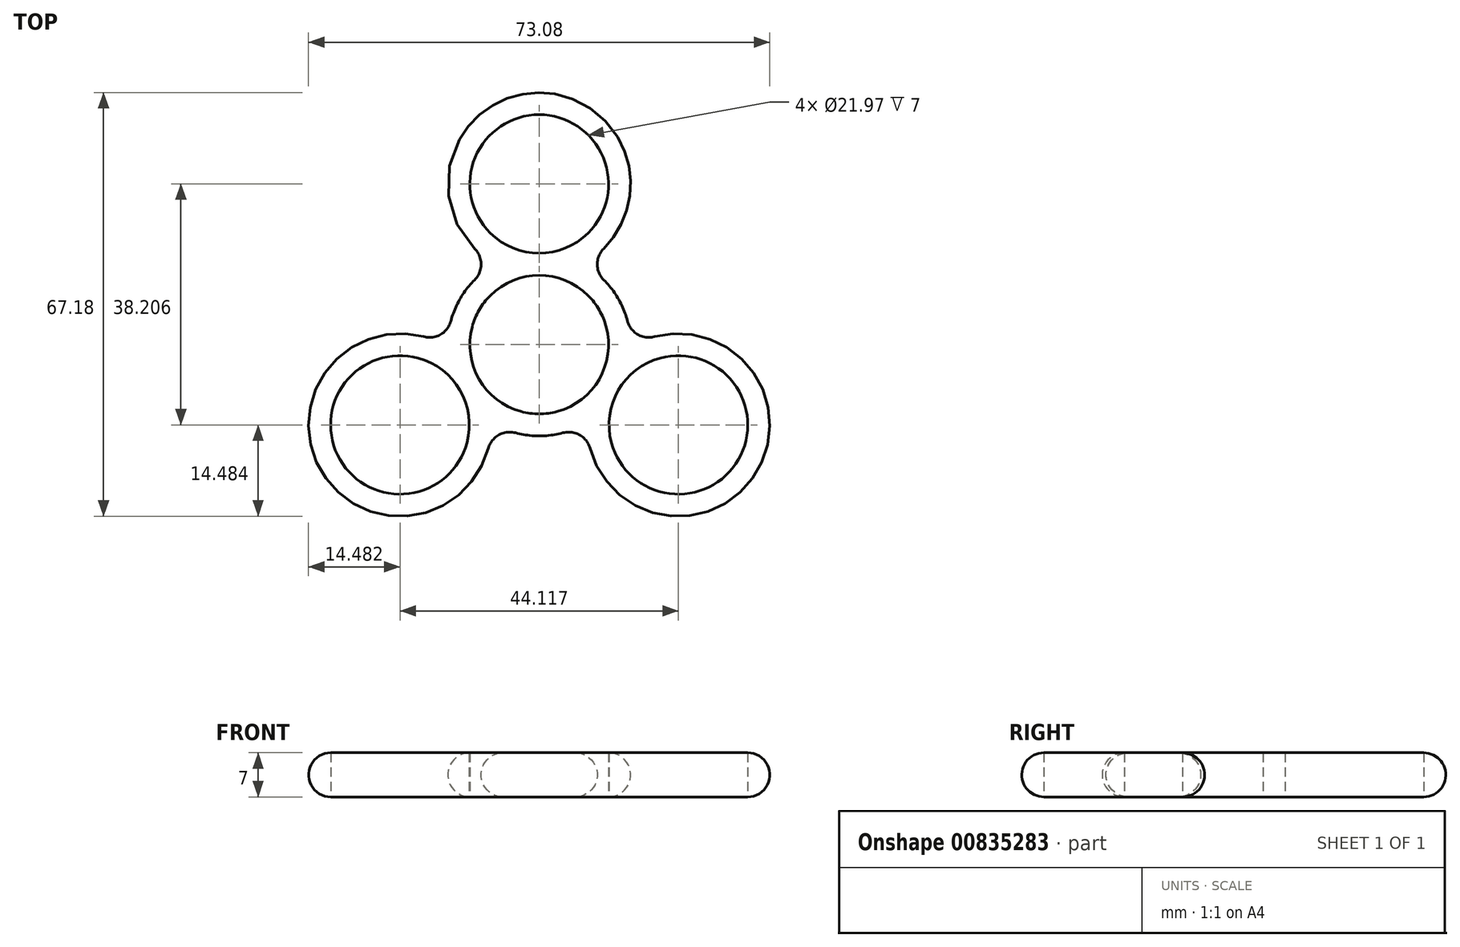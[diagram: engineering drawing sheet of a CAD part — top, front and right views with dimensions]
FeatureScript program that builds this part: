
annotation { "Feature Type Name" : "Feature", "Feature Type Description" : "" }
export const myFeature = defineFeature(function(context is Context, id is Id, definition is map)
    precondition{}
    {
        {
            var Q0;
            Q0=qCreatedBy(makeId("Top.planeOp"),FACE);
            var sketch = newSketch(context, id + "F0", { "sketchPlane" : qUnion([Q0])});
            skCircle(sketch, "E0", {"center": v(0, 0) * mm, "radius": 10.99 * mm});
            skCircle(sketch, "E1", {"center": v(0, 0) * mm, "radius": 25.47 * mm, "construction": true});
            skCircle(sketch, "E2", {"center": v(0, 25.47) * mm, "radius": 10.99 * mm});
            skCircle(sketch, "E3", {"center": v(-22.06, -12.74) * mm, "radius": 10.99 * mm});
            skCircle(sketch, "E4", {"center": v(22.06, -12.74) * mm, "radius": 10.99 * mm});
            skLineSegment(sketch, "E5", {"start": v(-22.06, -12.74) * mm, "end": v(22.06, -12.74) * mm, "construction": true});
            skLineSegment(sketch, "E6", {"start": v(0, 25.47) * mm, "end": v(-22.06, -12.74) * mm, "construction": true});
            skLineSegment(sketch, "E7", {"start": v(22.06, -12.74) * mm, "end": v(0, 25.47) * mm, "construction": true});
            skLineSegment(sketch, "E8.bottom", {"start": v(-57.15, 57.15) * mm, "end": v(57.15, 57.15) * mm, "construction": true});
            skLineSegment(sketch, "E8.top", {"start": v(-57.15, -57.15) * mm, "end": v(57.15, -57.15) * mm, "construction": true});
            skLineSegment(sketch, "E8.left", {"start": v(-57.15, 57.15) * mm, "end": v(-57.15, -57.15) * mm, "construction": true});
            skLineSegment(sketch, "E8.right", {"start": v(57.15, 57.15) * mm, "end": v(57.15, -57.15) * mm, "construction": true});
            skPoint(sketch, "E9", {"position": v(-57.15, 0) * mm});
            skPoint(sketch, "E10", {"position": v(0, 57.15) * mm});
            skArc(sketch, "E11", {"start": v(10.23, 15.21) * mm, "mid": v(0, 39.96) * mm, "end": v(-10.23, 15.21) * mm});
            skArc(sketch, "E12", {"start": v(8.06, -16.46) * mm, "mid": v(34.6, -19.98) * mm, "end": v(18.29, 1.25) * mm});
            skArc(sketch, "E13", {"start": v(-18.29, 1.25) * mm, "mid": v(-34.6, -19.98) * mm, "end": v(-8.06, -16.46) * mm});
            skArc(sketch, "E14", {"start": v(-10.23, 10.26) * mm, "mid": v(-12.54, 7.24) * mm, "end": v(-14, 3.73) * mm});
            skArc(sketch, "E15.trimOffspring", {"start": v(14, 3.73) * mm, "mid": v(12.54, 7.24) * mm, "end": v(10.23, 10.26) * mm});
            skArc(sketch, "E16.trimOffspring", {"start": v(-3.77, -13.99) * mm, "mid": v(0, -14.49) * mm, "end": v(3.77, -13.99) * mm});
            skPoint(sketch, "E17.visualSharp", {"position": v(-6.9, 12.74) * mm});
            skArc(sketch, "E17.filletArc", {"start": v(-10.23, 10.26) * mm, "mid": v(-9.2, 12.74) * mm, "end": v(-10.23, 15.21) * mm});
            skPoint(sketch, "E18.visualSharp", {"position": v(-14.48, -0.4) * mm});
            skArc(sketch, "E18.filletArc", {"start": v(-18.29, 1.25) * mm, "mid": v(-15.63, 1.6) * mm, "end": v(-14, 3.73) * mm});
            skPoint(sketch, "E19.visualSharp", {"position": v(-7.58, -12.35) * mm});
            skArc(sketch, "E19.filletArc", {"start": v(-3.77, -13.99) * mm, "mid": v(-6.43, -14.34) * mm, "end": v(-8.06, -16.46) * mm});
            skPoint(sketch, "E20.visualSharp", {"position": v(7.58, -12.35) * mm});
            skArc(sketch, "E20.filletArc", {"start": v(8.06, -16.46) * mm, "mid": v(6.43, -14.34) * mm, "end": v(3.77, -13.99) * mm});
            skPoint(sketch, "E21.visualSharp", {"position": v(14.48, -0.4) * mm});
            skArc(sketch, "E21.filletArc", {"start": v(14, 3.73) * mm, "mid": v(15.63, 1.6) * mm, "end": v(18.29, 1.25) * mm});
            skPoint(sketch, "E22.visualSharp", {"position": v(6.9, 12.74) * mm});
            skArc(sketch, "E22.filletArc", {"start": v(10.23, 15.21) * mm, "mid": v(9.2, 12.74) * mm, "end": v(10.23, 10.26) * mm});
            skSolve(sketch);
        }
        {
            var Q0;
            Q0 = qSketchRegion(id + "F0", true);
            extrude(context, id + "F1", {"entities" : qUnion([Q0]), "depth" : 7 * mm, "offsetDistance" : 25.4 * mm});
        }
        {
            var Q0;
            Q0=makeQuery(id+"F1.opExtrude","SWEPT_FACE",FACE,{"disambiguationData":[OSD([sQuery(id+"F0.wireOp",EDGE,"E12")])]});
            fillet(context, id + "F2", {"entities" : qUnion([Q0]), "radius" : 3.5 * mm, "tangentPropagation" : true, "allowEdgeOverflow" : false});
        }
    });
